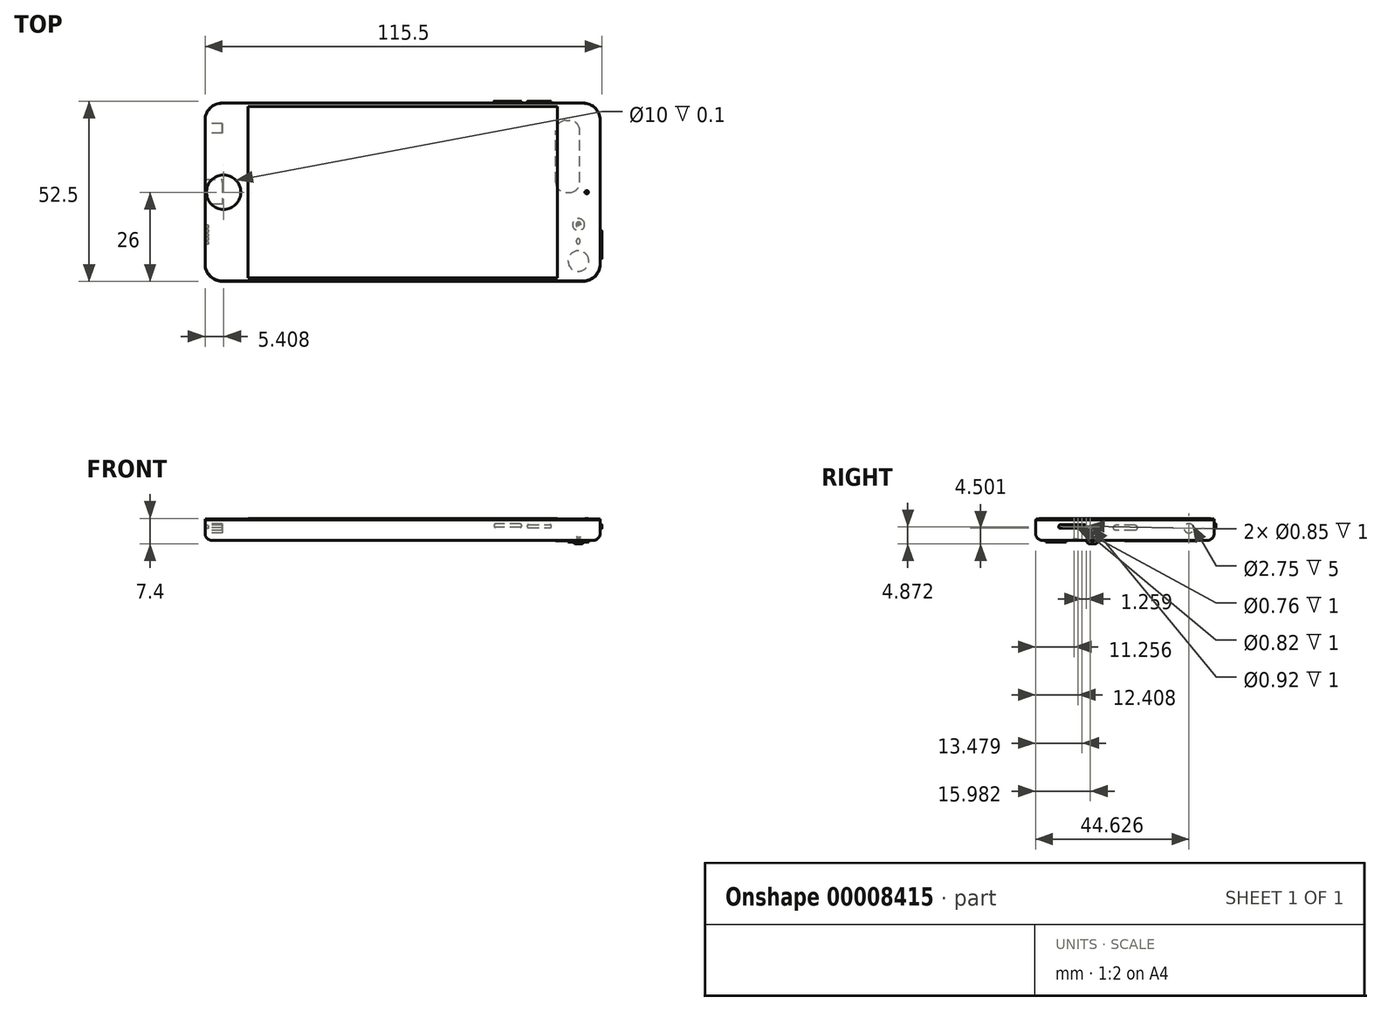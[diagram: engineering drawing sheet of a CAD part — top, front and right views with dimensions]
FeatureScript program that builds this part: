
annotation { "Feature Type Name" : "Feature", "Feature Type Description" : "" }
export const myFeature = defineFeature(function(context is Context, id is Id, definition is map)
    precondition{}
    {
        {
            var Q0;
            Q0=qCreatedBy(makeId("Top.planeOp"),FACE);
            var sketch = newSketch(context, id + "F0", { "sketchPlane" : qUnion([Q0])});
            skLineSegment(sketch, "E0.rect.bottom", {"start": v(-57.5, 26) * mm, "end": v(57.5, 26) * mm});
            skLineSegment(sketch, "E0.rect.top", {"start": v(-57.5, -26) * mm, "end": v(57.5, -26) * mm});
            skLineSegment(sketch, "E0.rect.left", {"start": v(-57.5, 26) * mm, "end": v(-57.5, -26) * mm});
            skLineSegment(sketch, "E0.rect.right", {"start": v(57.5, 26) * mm, "end": v(57.5, -26) * mm});
            skPoint(sketch, "E0.rect.middle", {"position": v(0, 0) * mm});
            skSolve(sketch);
        }
        {
            var Q0;
            Q0=makeQuery(id+"F0.imprint","IMPRINT",FACE,{"disambiguationData":[TD([[makeQuery(id+"F0.imprint","IMPRINT",EDGE,{"derivedFrom":sQuery(id+"F0.wireOp",EDGE,"E0.rect.bottom")}),-1.0]])]});
            extrude(context, id + "F1", {"entities" : qUnion([Q0]), "depth" : 6 * mm});
        }
        {
            var Q0;
            Q0=makeQuery(id+"F1.opExtrude","SWEPT_EDGE",EDGE,{"disambiguationData":[OSD([sQuery(id+"F0.wireOp",EDGE,"E0.rect.bottom"),sQuery(id+"F0.wireOp",EDGE,"E0.rect.right")])]});
            fillet(context, id + "F2", {"entities" : qUnion([Q0]), "radius" : 5 * mm, "tangentPropagation" : true, "allowEdgeOverflow" : false});
        }
        {
            var Q0;
            Q0=makeQuery(id+"F1.opExtrude","SWEPT_EDGE",EDGE,{"disambiguationData":[OSD([sQuery(id+"F0.wireOp",EDGE,"E0.rect.top"),sQuery(id+"F0.wireOp",EDGE,"E0.rect.right")])]});
            fillet(context, id + "F3", {"entities" : qUnion([Q0]), "radius" : 5 * mm, "tangentPropagation" : true, "allowEdgeOverflow" : false});
        }
        {
            var Q0;
            Q0=makeQuery(id+"F1.opExtrude","SWEPT_EDGE",EDGE,{"disambiguationData":[OSD([sQuery(id+"F0.wireOp",EDGE,"E0.rect.top"),sQuery(id+"F0.wireOp",EDGE,"E0.rect.left")])]});
            fillet(context, id + "F4", {"entities" : qUnion([Q0]), "radius" : 5 * mm, "tangentPropagation" : true, "allowEdgeOverflow" : false});
        }
        {
            var Q0;
            Q0=makeQuery(id+"F1.opExtrude","SWEPT_EDGE",EDGE,{"disambiguationData":[OSD([sQuery(id+"F0.wireOp",EDGE,"E0.rect.bottom"),sQuery(id+"F0.wireOp",EDGE,"E0.rect.left")])]});
            fillet(context, id + "F5", {"entities" : qUnion([Q0]), "radius" : 5 * mm, "tangentPropagation" : true, "allowEdgeOverflow" : false});
        }
        {
            var Q0;
            Q0=makeQuery(id+"F1.opExtrude","CAP_EDGE",EDGE,{"disambiguationData":[OSD([sQuery(id+"F0.wireOp",EDGE,"E0.rect.top")])],"isStart":true});
            fillet(context, id + "F6", {"entities" : qUnion([Q0]), "radius" : 2 * mm, "tangentPropagation" : true, "allowEdgeOverflow" : false});
        }
        {
            var Q0;
            Q0=makeQuery(id+"F1.opExtrude","SWEPT_FACE",FACE,{"disambiguationData":[OSD([sQuery(id+"F0.wireOp",EDGE,"E0.rect.bottom")])]});
            var sketch = newSketch(context, id + "F7", { "sketchPlane" : qUnion([Q0])});
            skLineSegment(sketch, "E1.right", {"start": v(-43.3, 3.62) * mm, "end": v(-43.3, 4.62) * mm});
            skLineSegment(sketch, "E2.0.MirrorCS", {"start": v(-36.3, 4.62) * mm, "end": v(-43.3, 4.62) * mm});
            skLineSegment(sketch, "E3.0.MirrorCS", {"start": v(-36.3, 3.62) * mm, "end": v(-36.3, 4.62) * mm});
            skLineSegment(sketch, "E4.0.MirrorCS", {"start": v(-36.3, 3.62) * mm, "end": v(-43.3, 3.62) * mm});
            skSolve(sketch);
        }
        {
            var Q0;
            Q0 = qSketchRegion(id + "F7", true);
            extrude(context, id + "F8", {"entities" : qUnion([Q0]), "operationType" : NewBodyOperationType.ADD, "depth" : .5 * mm});
        }
        {
            var Q0;
            Q0=makeQuery(id+"F8.opExtrude","SWEPT_EDGE",EDGE,{"disambiguationData":[OSD([sQuery(id+"F7.wireOp",EDGE,"E1.right"),sQuery(id+"F7.wireOp",EDGE,"E2.0.MirrorCS")])]});
            var Q1;
            Q1=makeQuery(id+"F8.opExtrude","SWEPT_EDGE",EDGE,{"disambiguationData":[OSD([sQuery(id+"F7.wireOp",EDGE,"E1.right"),sQuery(id+"F7.wireOp",EDGE,"E4.0.MirrorCS")])]});
            var Q2;
            Q2=makeQuery(id+"F8.opExtrude","SWEPT_EDGE",EDGE,{"disambiguationData":[OSD([sQuery(id+"F7.wireOp",EDGE,"E3.0.MirrorCS"),sQuery(id+"F7.wireOp",EDGE,"E4.0.MirrorCS")])]});
            var Q3;
            Q3=makeQuery(id+"F8.opExtrude","SWEPT_EDGE",EDGE,{"disambiguationData":[OSD([sQuery(id+"F7.wireOp",EDGE,"E2.0.MirrorCS"),sQuery(id+"F7.wireOp",EDGE,"E3.0.MirrorCS")])]});
            fillet(context, id + "F9", {"entities" : qUnion([Q0, Q1, Q2, Q3]), "radius" : .4 * mm, "tangentPropagation" : true, "allowEdgeOverflow" : false});
        }
        {
            var Q0;
            Q0=makeQuery(id+"F1.opExtrude","SWEPT_FACE",FACE,{"disambiguationData":[OSD([sQuery(id+"F0.wireOp",EDGE,"E0.rect.bottom")])]});
            var sketch = newSketch(context, id + "F10", { "sketchPlane" : qUnion([Q0])});
            skLineSegment(sketch, "E5.bottom", {"start": v(-34.62, 4.76) * mm, "end": v(-26.62, 4.76) * mm});
            skLineSegment(sketch, "E5.top", {"start": v(-34.62, 3.76) * mm, "end": v(-26.62, 3.76) * mm});
            skLineSegment(sketch, "E5.left", {"start": v(-34.62, 4.76) * mm, "end": v(-34.62, 3.76) * mm});
            skLineSegment(sketch, "E5.right", {"start": v(-26.62, 4.76) * mm, "end": v(-26.62, 3.76) * mm});
            skSolve(sketch);
        }
        {
            var Q0;
            Q0 = qSketchRegion(id + "F10", true);
            extrude(context, id + "F11", {"entities" : qUnion([Q0]), "operationType" : NewBodyOperationType.ADD, "depth" : .5 * mm});
        }
        {
            var Q0;
            Q0=makeQuery(id+"F11.opExtrude","SWEPT_EDGE",EDGE,{"disambiguationData":[OSD([sQuery(id+"F10.wireOp",EDGE,"E5.bottom"),sQuery(id+"F10.wireOp",EDGE,"E5.left")])]});
            var Q1;
            Q1=makeQuery(id+"F11.opExtrude","SWEPT_EDGE",EDGE,{"disambiguationData":[OSD([sQuery(id+"F10.wireOp",EDGE,"E5.top"),sQuery(id+"F10.wireOp",EDGE,"E5.left")])]});
            var Q2;
            Q2=makeQuery(id+"F11.opExtrude","SWEPT_EDGE",EDGE,{"disambiguationData":[OSD([sQuery(id+"F10.wireOp",EDGE,"E5.top"),sQuery(id+"F10.wireOp",EDGE,"E5.right")])]});
            var Q3;
            Q3=makeQuery(id+"F11.opExtrude","SWEPT_EDGE",EDGE,{"disambiguationData":[OSD([sQuery(id+"F10.wireOp",EDGE,"E5.bottom"),sQuery(id+"F10.wireOp",EDGE,"E5.right")])]});
            fillet(context, id + "F12", {"entities" : qUnion([Q0, Q1, Q2, Q3]), "radius" : .4 * mm, "tangentPropagation" : true, "allowEdgeOverflow" : false});
        }
        {
            var Q0;
            Q0=makeQuery(id+"F1.opExtrude","SWEPT_FACE",FACE,{"disambiguationData":[OSD([sQuery(id+"F0.wireOp",EDGE,"E0.rect.left")])]});
            var sketch = newSketch(context, id + "F13", { "sketchPlane" : qUnion([Q0])});
            skCircle(sketch, "E6", {"center": v(-18.63, 3.5) * mm, "radius": 1.38 * mm});
            skSolve(sketch);
        }
        {
            var Q0;
            Q0 = qSketchRegion(id + "F13", true);
            extrude(context, id + "F14", {"entities" : qUnion([Q0]), "operationType" : NewBodyOperationType.REMOVE, "oppositeDirection" : true, "depth" : 5 * mm});
        }
        {
            var Q0;
            Q0=makeQuery(id+"F1.opExtrude","SWEPT_FACE",FACE,{"disambiguationData":[OSD([sQuery(id+"F0.wireOp",EDGE,"E0.rect.left")])]});
            var sketch = newSketch(context, id + "F15", { "sketchPlane" : qUnion([Q0])});
            skLineSegment(sketch, "E7.bottom", {"start": v(-3.75, 4.39) * mm, "end": v(3.47, 4.39) * mm});
            skLineSegment(sketch, "E7.top", {"start": v(-3.75, 2.97) * mm, "end": v(3.47, 2.97) * mm});
            skLineSegment(sketch, "E7.left", {"start": v(-3.75, 4.39) * mm, "end": v(-3.75, 2.97) * mm});
            skLineSegment(sketch, "E7.right", {"start": v(3.47, 4.39) * mm, "end": v(3.47, 2.97) * mm});
            skSolve(sketch);
        }
        {
            var Q0;
            Q0=makeQuery(id+"F15.imprint","IMPRINT",FACE,{"disambiguationData":[TD([[makeQuery(id+"F15.imprint","IMPRINT",EDGE,{"derivedFrom":sQuery(id+"F15.wireOp",EDGE,"E7.bottom")}),-1.0]])]});
            extrude(context, id + "F16", {"entities" : qUnion([Q0]), "operationType" : NewBodyOperationType.REMOVE, "oppositeDirection" : true, "depth" : 5 * mm});
        }
        {
            var Q0;
            Q0=makeQuery(id+"F16.boolean.opBoolean","COPY",EDGE,{"derivedFrom":makeQuery(id+"F16.opExtrude","SWEPT_EDGE",EDGE,{"disambiguationData":[OSD([sQuery(id+"F15.wireOp",EDGE,"E7.bottom"),sQuery(id+"F15.wireOp",EDGE,"E7.left")])]})});
            var Q1;
            Q1=makeQuery(id+"F16.boolean.opBoolean","COPY",EDGE,{"derivedFrom":makeQuery(id+"F16.opExtrude","SWEPT_EDGE",EDGE,{"disambiguationData":[OSD([sQuery(id+"F15.wireOp",EDGE,"E7.top"),sQuery(id+"F15.wireOp",EDGE,"E7.left")])]})});
            var Q2;
            Q2=makeQuery(id+"F16.boolean.opBoolean","COPY",EDGE,{"derivedFrom":makeQuery(id+"F16.opExtrude","SWEPT_EDGE",EDGE,{"disambiguationData":[OSD([sQuery(id+"F15.wireOp",EDGE,"E7.bottom"),sQuery(id+"F15.wireOp",EDGE,"E7.right")])]})});
            var Q3;
            Q3=makeQuery(id+"F16.boolean.opBoolean","COPY",EDGE,{"derivedFrom":makeQuery(id+"F16.opExtrude","SWEPT_EDGE",EDGE,{"disambiguationData":[OSD([sQuery(id+"F15.wireOp",EDGE,"E7.top"),sQuery(id+"F15.wireOp",EDGE,"E7.right")])]})});
            fillet(context, id + "F17", {"entities" : qUnion([Q0, Q1, Q2, Q3]), "radius" : .9 * mm, "tangentPropagation" : true, "allowEdgeOverflow" : false});
        }
        {
            var Q0;
            Q0=makeQuery(id+"F1.opExtrude","SWEPT_FACE",FACE,{"disambiguationData":[OSD([sQuery(id+"F0.wireOp",EDGE,"E0.rect.left")])]});
            var sketch = newSketch(context, id + "F18", { "sketchPlane" : qUnion([Q0])});
            skCircle(sketch, "E8", {"center": v(10.02, 3.87) * mm, "radius": 0.46 * mm});
            skCircle(sketch, "E9", {"center": v(11.26, 3.87) * mm, "radius": 0.42 * mm});
            skCircle(sketch, "E10", {"center": v(12.52, 3.87) * mm, "radius": 0.42 * mm});
            skCircle(sketch, "E11", {"center": v(13.6, 3.87) * mm, "radius": 0.41 * mm});
            skCircle(sketch, "E12", {"center": v(14.74, 3.87) * mm, "radius": 0.38 * mm});
            skSolve(sketch);
        }
        {
            var Q0;
            Q0 = qSketchRegion(id + "F18", true);
            extrude(context, id + "F19", {"entities" : qUnion([Q0]), "operationType" : NewBodyOperationType.REMOVE, "oppositeDirection" : true, "depth" : 1 * mm});
        }
        {
            var Q0;
            Q0=makeQuery(id+"F1.opExtrude","SWEPT_FACE",FACE,{"disambiguationData":[OSD([sQuery(id+"F0.wireOp",EDGE,"E0.rect.right")])]});
            var sketch = newSketch(context, id + "F20", { "sketchPlane" : qUnion([Q0])});
            skLineSegment(sketch, "E13.bottom", {"start": v(-19.26, 4.51) * mm, "end": v(-11.26, 4.51) * mm});
            skLineSegment(sketch, "E13.top", {"start": v(-19.26, 3.51) * mm, "end": v(-11.26, 3.51) * mm});
            skLineSegment(sketch, "E13.left", {"start": v(-19.26, 4.51) * mm, "end": v(-19.26, 3.51) * mm});
            skLineSegment(sketch, "E13.right", {"start": v(-11.26, 4.51) * mm, "end": v(-11.26, 3.51) * mm});
            skSolve(sketch);
        }
        {
            var Q0;
            Q0=makeQuery(id+"F20.imprint","IMPRINT",FACE,{"disambiguationData":[TD([[makeQuery(id+"F20.imprint","IMPRINT",EDGE,{"derivedFrom":sQuery(id+"F20.wireOp",EDGE,"E13.bottom")}),-1.0]])]});
            extrude(context, id + "F21", {"entities" : qUnion([Q0]), "operationType" : NewBodyOperationType.ADD, "depth" : .5 * mm});
        }
        {
            var Q0;
            Q0=makeQuery(id+"F21.opExtrude","SWEPT_EDGE",EDGE,{"disambiguationData":[OSD([sQuery(id+"F20.wireOp",EDGE,"E13.bottom"),sQuery(id+"F20.wireOp",EDGE,"E13.left")])]});
            var Q1;
            Q1=makeQuery(id+"F21.opExtrude","SWEPT_EDGE",EDGE,{"disambiguationData":[OSD([sQuery(id+"F20.wireOp",EDGE,"E13.top"),sQuery(id+"F20.wireOp",EDGE,"E13.left")])]});
            var Q2;
            Q2=makeQuery(id+"F21.opExtrude","SWEPT_EDGE",EDGE,{"disambiguationData":[OSD([sQuery(id+"F20.wireOp",EDGE,"E13.bottom"),sQuery(id+"F20.wireOp",EDGE,"E13.right")])]});
            var Q3;
            Q3=makeQuery(id+"F21.opExtrude","SWEPT_EDGE",EDGE,{"disambiguationData":[OSD([sQuery(id+"F20.wireOp",EDGE,"E13.top"),sQuery(id+"F20.wireOp",EDGE,"E13.right")])]});
            fillet(context, id + "F22", {"entities" : qUnion([Q0, Q1, Q2, Q3]), "radius" : .4 * mm, "tangentPropagation" : true, "allowEdgeOverflow" : false});
        }
        {
            var Q0;
            Q0=makeQuery(id+"F1.opExtrude","CAP_FACE",FACE,{"disambiguationData":[OSD([sQuery(id+"F0.wireOp",EDGE,"E0.rect.bottom"),sQuery(id+"F0.wireOp",EDGE,"E0.rect.top"),sQuery(id+"F0.wireOp",EDGE,"E0.rect.left"),sQuery(id+"F0.wireOp",EDGE,"E0.rect.right")])],"isStart":true});
            var sketch = newSketch(context, id + "F23", { "sketchPlane" : qUnion([Q0])});
            skCircle(sketch, "E14", {"center": v(51.16, 20.04) * mm, "radius": 3 * mm});
            skSolve(sketch);
        }
        {
            var Q0;
            Q0=makeQuery(id+"F23.imprint","IMPRINT",FACE,{"disambiguationData":[TD([[makeQuery(id+"F23.imprint","IMPRINT",EDGE,{"derivedFrom":sQuery(id+"F23.wireOp",EDGE,"E14")}),1.0]])]});
            extrude(context, id + "F24", {"entities" : qUnion([Q0]), "depth" : .5 * mm});
        }
        {
            var Q0;
            Q0=makeQuery(id+"F1.opExtrude","CAP_FACE",FACE,{"disambiguationData":[OSD([sQuery(id+"F0.wireOp",EDGE,"E0.rect.bottom"),sQuery(id+"F0.wireOp",EDGE,"E0.rect.top"),sQuery(id+"F0.wireOp",EDGE,"E0.rect.left"),sQuery(id+"F0.wireOp",EDGE,"E0.rect.right")])],"isStart":true});
            var sketch = newSketch(context, id + "F25", { "sketchPlane" : qUnion([Q0])});
            skLineSegment(sketch, "E15.rect.bottom", {"start": v(50.61, 15.04) * mm, "end": v(51.61, 15.04) * mm});
            skLineSegment(sketch, "E15.rect.top", {"start": v(50.61, 13.54) * mm, "end": v(51.61, 13.54) * mm});
            skLineSegment(sketch, "E15.rect.left", {"start": v(50.61, 15.04) * mm, "end": v(50.61, 13.54) * mm});
            skLineSegment(sketch, "E15.rect.right", {"start": v(51.61, 15.04) * mm, "end": v(51.61, 13.54) * mm});
            skPoint(sketch, "E15.rect.middle", {"position": v(51.11, 14.3) * mm});
            skSolve(sketch);
        }
        {
            var Q0;
            Q0 = qSketchRegion(id + "F25", true);
            extrude(context, id + "F26", {"entities" : qUnion([Q0]), "operationType" : NewBodyOperationType.REMOVE, "oppositeDirection" : true, "depth" : .5 * mm});
        }
        {
            var Q0;
            Q0=makeQuery(id+"F26.boolean.opBoolean","COPY",EDGE,{"derivedFrom":makeQuery(id+"F26.opExtrude","SWEPT_EDGE",EDGE,{"disambiguationData":[OSD([sQuery(id+"F25.wireOp",EDGE,"E15.rect.top"),sQuery(id+"F25.wireOp",EDGE,"E15.rect.left")])]})});
            var Q1;
            Q1=makeQuery(id+"F26.boolean.opBoolean","COPY",EDGE,{"derivedFrom":makeQuery(id+"F26.opExtrude","SWEPT_EDGE",EDGE,{"disambiguationData":[OSD([sQuery(id+"F25.wireOp",EDGE,"E15.rect.bottom"),sQuery(id+"F25.wireOp",EDGE,"E15.rect.left")])]})});
            var Q2;
            Q2=makeQuery(id+"F26.boolean.opBoolean","COPY",EDGE,{"derivedFrom":makeQuery(id+"F26.opExtrude","SWEPT_EDGE",EDGE,{"disambiguationData":[OSD([sQuery(id+"F25.wireOp",EDGE,"E15.rect.bottom"),sQuery(id+"F25.wireOp",EDGE,"E15.rect.right")])]})});
            var Q3;
            Q3=makeQuery(id+"F26.boolean.opBoolean","COPY",EDGE,{"derivedFrom":makeQuery(id+"F26.opExtrude","SWEPT_EDGE",EDGE,{"disambiguationData":[OSD([sQuery(id+"F25.wireOp",EDGE,"E15.rect.top"),sQuery(id+"F25.wireOp",EDGE,"E15.rect.right")])]})});
            fillet(context, id + "F27", {"entities" : qUnion([Q0, Q1, Q2, Q3]), "radius" : .5 * mm, "tangentPropagation" : true, "allowEdgeOverflow" : false});
        }
        {
            var Q0;
            Q0=makeQuery(id+"F1.opExtrude","CAP_FACE",FACE,{"disambiguationData":[OSD([sQuery(id+"F0.wireOp",EDGE,"E0.rect.bottom"),sQuery(id+"F0.wireOp",EDGE,"E0.rect.top"),sQuery(id+"F0.wireOp",EDGE,"E0.rect.left"),sQuery(id+"F0.wireOp",EDGE,"E0.rect.right")])],"isStart":true});
            var sketch = newSketch(context, id + "F28", { "sketchPlane" : qUnion([Q0])});
            skCircle(sketch, "E16", {"center": v(51.2, 9.45) * mm, "radius": 1.75 * mm});
            skSolve(sketch);
        }
        {
            var Q0;
            Q0 = qSketchRegion(id + "F28", true);
            extrude(context, id + "F29", {"entities" : qUnion([Q0]), "operationType" : NewBodyOperationType.REMOVE, "oppositeDirection" : true, "depth" : 1 * mm});
        }
        {
            var Q0;
            Q0=makeQuery(id+"F29.boolean.opBoolean","COPY",EDGE,{"derivedFrom":makeQuery(id+"F29.opExtrude","CAP_EDGE",EDGE,{"disambiguationData":[OSD([sQuery(id+"F28.wireOp",EDGE,"E16")])],"isStart":false})});
            fillet(context, id + "F30", {"entities" : qUnion([Q0]), "radius" : 1 * mm, "tangentPropagation" : true, "allowEdgeOverflow" : false});
        }
        {
            var Q0;
            Q0=makeQuery(id+"F1.opExtrude","CAP_FACE",FACE,{"disambiguationData":[OSD([sQuery(id+"F0.wireOp",EDGE,"E0.rect.bottom"),sQuery(id+"F0.wireOp",EDGE,"E0.rect.top"),sQuery(id+"F0.wireOp",EDGE,"E0.rect.left"),sQuery(id+"F0.wireOp",EDGE,"E0.rect.right")])],"isStart":true});
            var sketch = newSketch(context, id + "F31", { "sketchPlane" : qUnion([Q0])});
            skLineSegment(sketch, "E17.rect.bottom", {"start": v(44.56, 0.08) * mm, "end": v(51.56, 0.08) * mm});
            skLineSegment(sketch, "E17.rect.top", {"start": v(44.56, -20.92) * mm, "end": v(51.56, -20.92) * mm});
            skLineSegment(sketch, "E17.rect.left", {"start": v(44.56, 0.08) * mm, "end": v(44.56, -20.92) * mm});
            skLineSegment(sketch, "E17.rect.right", {"start": v(51.56, 0.08) * mm, "end": v(51.56, -20.92) * mm});
            skPoint(sketch, "E17.rect.middle", {"position": v(48.06, -10.42) * mm});
            skSolve(sketch);
        }
        {
            var Q0;
            Q0=makeQuery(id+"F31.imprint","IMPRINT",FACE,{"disambiguationData":[TD([[makeQuery(id+"F31.imprint","IMPRINT",EDGE,{"derivedFrom":sQuery(id+"F31.wireOp",EDGE,"E17.rect.bottom")}),-1.0]])]});
            var Q1;
            Q1=sQuery(id+"F31.wireOp",EDGE,"E17.rect.right");
            extrude(context, id + "F32", {"entities" : qUnion([Q0]), "surfaceEntities" : qUnion([Q1]), "depth" : 0.1 * mm});
        }
        {
            var Q0;
            Q0=makeQuery(id+"F32.opExtrude","SWEPT_EDGE",EDGE,{"disambiguationData":[OSD([sQuery(id+"F31.wireOp",EDGE,"E17.rect.top"),sQuery(id+"F31.wireOp",EDGE,"E17.rect.right")])]});
            var Q1;
            Q1=makeQuery(id+"F32.opExtrude","SWEPT_EDGE",EDGE,{"disambiguationData":[OSD([sQuery(id+"F31.wireOp",EDGE,"E17.rect.top"),sQuery(id+"F31.wireOp",EDGE,"E17.rect.left")])]});
            var Q2;
            Q2=makeQuery(id+"F32.opExtrude","SWEPT_EDGE",EDGE,{"disambiguationData":[OSD([sQuery(id+"F31.wireOp",EDGE,"E17.rect.bottom"),sQuery(id+"F31.wireOp",EDGE,"E17.rect.right")])]});
            var Q3;
            Q3=makeQuery(id+"F32.opExtrude","SWEPT_EDGE",EDGE,{"disambiguationData":[OSD([sQuery(id+"F31.wireOp",EDGE,"E17.rect.bottom"),sQuery(id+"F31.wireOp",EDGE,"E17.rect.left")])]});
            fillet(context, id + "F33", {"entities" : qUnion([Q0, Q1, Q2, Q3]), "radius" : 3 * mm, "tangentPropagation" : true, "allowEdgeOverflow" : false});
        }
        {
            var Q0;
            Q0=makeQuery(id+"F1.opExtrude","CAP_FACE",FACE,{"disambiguationData":[OSD([sQuery(id+"F0.wireOp",EDGE,"E0.rect.bottom"),sQuery(id+"F0.wireOp",EDGE,"E0.rect.top"),sQuery(id+"F0.wireOp",EDGE,"E0.rect.left"),sQuery(id+"F0.wireOp",EDGE,"E0.rect.right")])],"isStart":false});
            var sketch = newSketch(context, id + "F34", { "sketchPlane" : qUnion([Q0])});
            skLineSegment(sketch, "E18.bottom", {"start": v(57.5, -25.82) * mm, "end": v(-57.5, -25.82) * mm});
            skLineSegment(sketch, "E18.top", {"start": v(57.5, 25.93) * mm, "end": v(-57.5, 25.93) * mm});
            skLineSegment(sketch, "E18.left", {"start": v(57.5, -25.82) * mm, "end": v(57.5, 25.93) * mm});
            skLineSegment(sketch, "E18.right", {"start": v(-57.5, -25.82) * mm, "end": v(-57.5, 25.93) * mm});
            skSolve(sketch);
        }
        {
            var Q0;
            Q0 = qSketchRegion(id + "F34", true);
            extrude(context, id + "F35", {"entities" : qUnion([Q0]), "depth" : 0.2 * mm});
        }
        {
            var Q0;
            Q0=makeQuery(id+"F35.opExtrude","SWEPT_EDGE",EDGE,{"disambiguationData":[OSD([sQuery(id+"F34.wireOp",EDGE,"E18.top"),sQuery(id+"F34.wireOp",EDGE,"E18.right")])]});
            var Q1;
            Q1=makeQuery(id+"F35.opExtrude","SWEPT_EDGE",EDGE,{"disambiguationData":[OSD([sQuery(id+"F34.wireOp",EDGE,"E18.top"),sQuery(id+"F34.wireOp",EDGE,"E18.left")])]});
            var Q2;
            Q2=makeQuery(id+"F35.opExtrude","SWEPT_EDGE",EDGE,{"disambiguationData":[OSD([sQuery(id+"F34.wireOp",EDGE,"E18.bottom"),sQuery(id+"F34.wireOp",EDGE,"E18.left")])]});
            var Q3;
            Q3=makeQuery(id+"F35.opExtrude","SWEPT_EDGE",EDGE,{"disambiguationData":[OSD([sQuery(id+"F34.wireOp",EDGE,"E18.bottom"),sQuery(id+"F34.wireOp",EDGE,"E18.right")])]});
            fillet(context, id + "F36", {"entities" : qUnion([Q0, Q1, Q2, Q3]), "radius" : 5 * mm, "tangentPropagation" : true, "allowEdgeOverflow" : false});
        }
        {
            var Q0;
            Q0=makeQuery(id+"F35.opExtrude","CAP_FACE",FACE,{"disambiguationData":[OSD([sQuery(id+"F34.wireOp",EDGE,"E18.bottom"),sQuery(id+"F34.wireOp",EDGE,"E18.top"),sQuery(id+"F34.wireOp",EDGE,"E18.left"),sQuery(id+"F34.wireOp",EDGE,"E18.right")])],"isStart":false});
            var sketch = newSketch(context, id + "F37", { "sketchPlane" : qUnion([Q0])});
            skSolve(sketch);
        }
        {
            var Q0;
            {var subQ3=sQuery(id+"F34.wireOp",EDGE,"E18.bottom");Q0=makeQuery(id+"F37.imprint","IMPRINT",FACE,{"disambiguationData":[TD([[makeQuery(id+"F37.imprint","IMPRINT",EDGE,{"derivedFrom":makeQuery(id+"F35.opExtrude","CAP_EDGE",EDGE,{"disambiguationData":[OSD([subQ3])],"isStart":false})}),-1.0]])]});}
            var sketch = newSketch(context, id + "F38", { "sketchPlane" : qUnion([Q0])});
            skCircle(sketch, "E19", {"center": v(53.58, 0) * mm, "radius": 0.5 * mm});
            skSolve(sketch);
        }
        {
            var Q0;
            Q0 = qSketchRegion(id + "F38", true);
            extrude(context, id + "F39", {"entities" : qUnion([Q0]), "depth" : 0.2 * mm});
        }
        {
            var Q0;
            {var subQ3=sQuery(id+"F34.wireOp",EDGE,"E18.bottom");Q0=makeQuery(id+"F37.imprint","IMPRINT",FACE,{"disambiguationData":[TD([[makeQuery(id+"F37.imprint","IMPRINT",EDGE,{"derivedFrom":makeQuery(id+"F35.opExtrude","CAP_EDGE",EDGE,{"disambiguationData":[OSD([subQ3])],"isStart":false})}),-1.0]])]});}
            var sketch = newSketch(context, id + "F40", { "sketchPlane" : qUnion([Q0])});
            skLineSegment(sketch, "E20.rect.bottom", {"start": v(-45, 25) * mm, "end": v(45, 25) * mm});
            skLineSegment(sketch, "E20.rect.top", {"start": v(-45, -25) * mm, "end": v(45, -25) * mm});
            skLineSegment(sketch, "E20.rect.left", {"start": v(-45, 25) * mm, "end": v(-45, -25) * mm});
            skLineSegment(sketch, "E20.rect.right", {"start": v(45, 25) * mm, "end": v(45, -25) * mm});
            skPoint(sketch, "E20.rect.middle", {"position": v(0, 0) * mm});
            skSolve(sketch);
        }
        {
            var Q0;
            Q0 = qSketchRegion(id + "F40", true);
            extrude(context, id + "F41", {"entities" : qUnion([Q0]), "depth" : 0.1 * mm});
        }
        {
            var Q0;
            {var subQ3=sQuery(id+"F34.wireOp",EDGE,"E18.bottom");Q0=makeQuery(id+"F37.imprint","IMPRINT",FACE,{"disambiguationData":[TD([[makeQuery(id+"F37.imprint","IMPRINT",EDGE,{"derivedFrom":makeQuery(id+"F35.opExtrude","CAP_EDGE",EDGE,{"disambiguationData":[OSD([subQ3])],"isStart":false})}),-1.0]])]});}
            var sketch = newSketch(context, id + "F42", { "sketchPlane" : qUnion([Q0])});
            skCircle(sketch, "E21", {"center": v(-52.1, 0) * mm, "radius": 5 * mm});
            skSolve(sketch);
        }
        {
            var Q0;
            Q0 = qSketchRegion(id + "F42", true);
            var Q1;
            Q1=sQuery(id+"F42.wireOp",EDGE,"E21");
            extrude(context, id + "F43", {"entities" : qUnion([Q0]), "operationType" : NewBodyOperationType.REMOVE, "surfaceEntities" : qUnion([Q1]), "oppositeDirection" : true, "depth" : .1 * mm});
        }
    });
